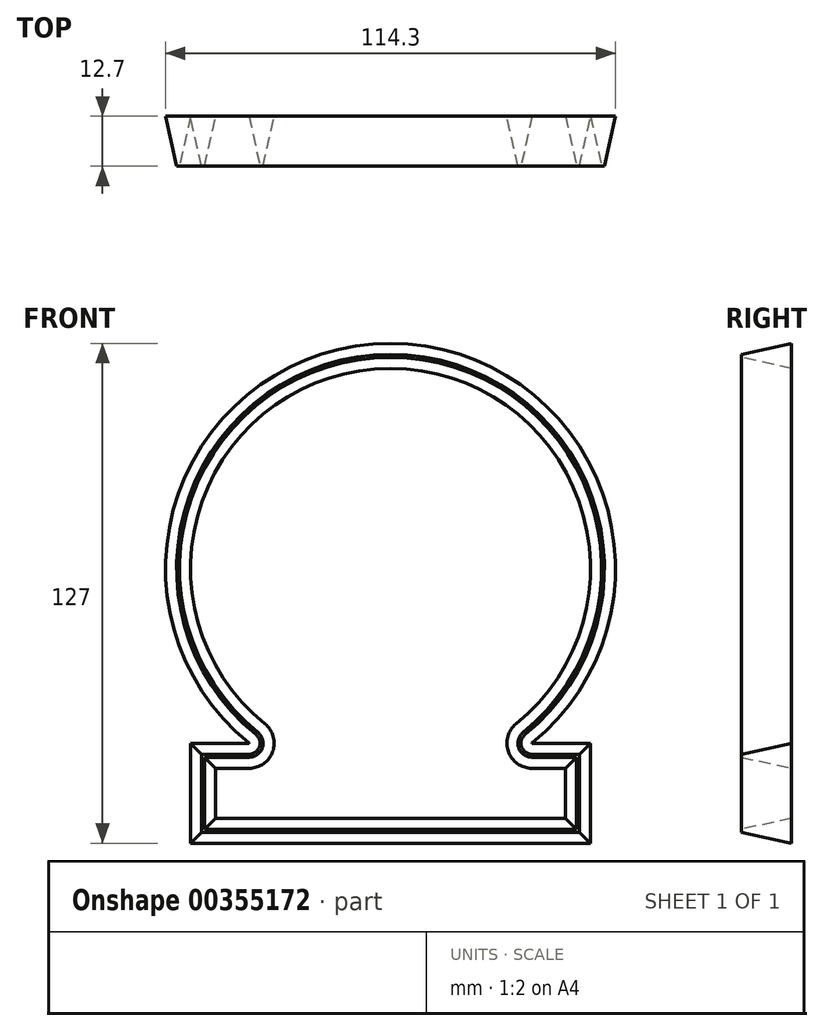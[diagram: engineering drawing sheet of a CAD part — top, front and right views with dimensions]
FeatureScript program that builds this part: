
annotation { "Feature Type Name" : "Feature", "Feature Type Description" : "" }
export const myFeature = defineFeature(function(context is Context, id is Id, definition is map)
    precondition{}
    {
        {
            var Q0;
            Q0=qCreatedBy(makeId("Front.planeOp"),FACE);
            var sketch = newSketch(context, id + "F0", { "sketchPlane" : qUnion([Q0])});
            skArc(sketch, "E0", {"start": v(31.93, -39.51) * mm, "mid": v(0, 50.8) * mm, "end": v(-31.93, -39.51) * mm});
            skLineSegment(sketch, "E1.bottom", {"start": v(-44.45, -63.5) * mm, "end": v(44.45, -63.5) * mm});
            skLineSegment(sketch, "E1.top", {"start": v(-44.45, -50.8) * mm, "end": v(-35.92, -50.8) * mm});
            skLineSegment(sketch, "E1.left", {"start": v(-44.45, -63.5) * mm, "end": v(-44.45, -50.8) * mm});
            skLineSegment(sketch, "E1.right", {"start": v(44.45, -63.5) * mm, "end": v(44.45, -50.8) * mm});
            skPoint(sketch, "E1.middle", {"position": v(0, -57.15) * mm});
            skArc(sketch, "E2", {"start": v(-35.92, -50.8) * mm, "mid": v(-29.93, -46.57) * mm, "end": v(-31.93, -39.51) * mm});
            skArc(sketch, "E3", {"start": v(31.93, -39.51) * mm, "mid": v(29.93, -46.57) * mm, "end": v(35.92, -50.8) * mm});
            skLineSegment(sketch, "E4", {"start": v(-31.93, -39.51) * mm, "end": v(31.93, -39.51) * mm, "construction": true});
            skLineSegment(sketch, "E5.trimOffspring", {"start": v(35.92, -50.8) * mm, "end": v(44.45, -50.8) * mm});
            skLineSegment(sketch, "E6.0", {"start": v(36, -44.45) * mm, "end": v(50.8, -44.45) * mm});
            skLineSegment(sketch, "E6.1", {"start": v(-50.8, -44.45) * mm, "end": v(-36, -44.45) * mm});
            skLineSegment(sketch, "E6.2", {"start": v(-50.8, -69.85) * mm, "end": v(-50.8, -44.45) * mm});
            skArc(sketch, "E6.3", {"start": v(35.98, -44.4) * mm, "mid": v(0, 57.15) * mm, "end": v(-35.98, -44.4) * mm});
            skLineSegment(sketch, "E6.4", {"start": v(-50.8, -69.85) * mm, "end": v(50.8, -69.85) * mm});
            skLineSegment(sketch, "E6.5", {"start": v(50.8, -69.85) * mm, "end": v(50.8, -44.45) * mm});
            skArc(sketch, "E7.filletArc", {"start": v(-36, -44.45) * mm, "mid": v(-35.97, -44.43) * mm, "end": v(-35.98, -44.4) * mm});
            skArc(sketch, "E8.filletArc", {"start": v(35.98, -44.4) * mm, "mid": v(35.97, -44.43) * mm, "end": v(36, -44.45) * mm});
            skSolve(sketch);
        }
        {
            var Q0;
            Q0 = qSketchRegion(id + "F0", true);
            extrude(context, id + "F1", {"entities" : qUnion([Q0]), "depth" : 12.7 * mm, "hasDraft" : true, "draftAngle" : 12.5 * degree, "draftPullDirection" : true});
        }
    });
